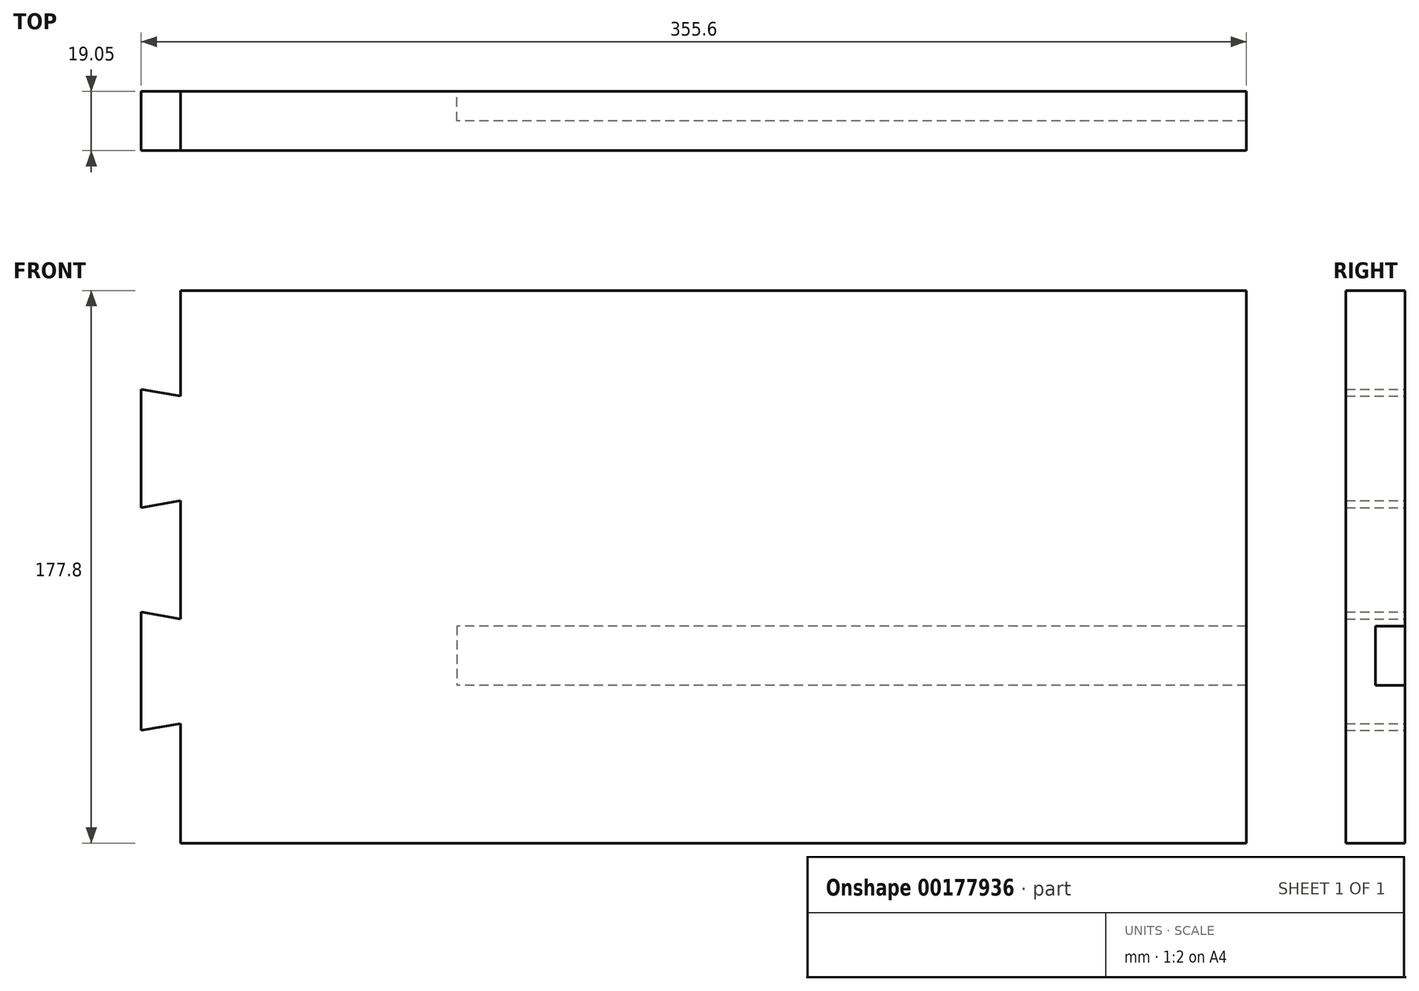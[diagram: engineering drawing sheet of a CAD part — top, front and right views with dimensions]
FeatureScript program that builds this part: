
annotation { "Feature Type Name" : "Feature", "Feature Type Description" : "" }
export const myFeature = defineFeature(function(context is Context, id is Id, definition is map)
    precondition{}
    {
        {
            var Q0;
            Q0=qCreatedBy(makeId("Front.planeOp"),FACE);
            var sketch = newSketch(context, id + "F0", { "sketchPlane" : qUnion([Q0])});
            skLineSegment(sketch, "E0.bottom", {"start": v(0, 0) * mm, "end": v(355.6, 0) * mm});
            skLineSegment(sketch, "E0.top", {"start": v(12.7, 177.8) * mm, "end": v(355.6, 177.8) * mm});
            skLineSegment(sketch, "E0.left", {"start": v(0, 36.23) * mm, "end": v(0, 74.33) * mm});
            skLineSegment(sketch, "E0.right", {"start": v(355.6, 0) * mm, "end": v(355.6, 177.8) * mm});
            skLineSegment(sketch, "E1", {"start": v(12.7, 177.8) * mm, "end": v(12.7, 143.81) * mm});
            skLineSegment(sketch, "E2", {"start": v(0, 146.05) * mm, "end": v(12.7, 143.81) * mm});
            skLineSegment(sketch, "E3", {"start": v(12.7, 110.19) * mm, "end": v(0, 107.95) * mm});
            skPoint(sketch, "E4", {"position": v(0, 88.9) * mm});
            skLineSegment(sketch, "E5", {"start": v(0, 74.33) * mm, "end": v(12.7, 72.09) * mm});
            skLineSegment(sketch, "E6", {"start": v(12.7, 38.47) * mm, "end": v(0, 36.23) * mm});
            skLineSegment(sketch, "E7.trimOffspring", {"start": v(12.7, 110.19) * mm, "end": v(12.7, 72.09) * mm});
            skLineSegment(sketch, "E8.trimOffspring", {"start": v(12.7, 38.47) * mm, "end": v(12.7, 0) * mm});
            skPoint(sketch, "E9.orphan", {"position": v(0, 177.8) * mm});
            skLineSegment(sketch, "E10.trimOffspring", {"start": v(0, 107.95) * mm, "end": v(0, 146.05) * mm});
            skSolve(sketch);
        }
        {
            var Q0;
            Q0=makeQuery(id+"F0.imprint","IMPRINT",FACE,{"disambiguationData":[TD([[makeQuery(id+"F0.imprint","IMPRINT",EDGE,{"derivedFrom":sQuery(id+"F0.wireOp",EDGE,"E0.bottom")}),1.0]])]});
            extrude(context, id + "F1", {"entities" : qUnion([Q0]), "depth" : 19.05 * mm});
        }
        {
            var Q0;
            Q0=makeQuery(id+"F1.opExtrude","CAP_FACE",FACE,{"disambiguationData":[OSD([sQuery(id+"F0.wireOp",EDGE,"E0.bottom"),sQuery(id+"F0.wireOp",EDGE,"E0.top"),sQuery(id+"F0.wireOp",EDGE,"E0.left"),sQuery(id+"F0.wireOp",EDGE,"E0.right"),sQuery(id+"F0.wireOp",EDGE,"E1"),sQuery(id+"F0.wireOp",EDGE,"E2"),sQuery(id+"F0.wireOp",EDGE,"E3"),sQuery(id+"F0.wireOp",EDGE,"E5"),sQuery(id+"F0.wireOp",EDGE,"E6"),sQuery(id+"F0.wireOp",EDGE,"E7.trimOffspring"),sQuery(id+"F0.wireOp",EDGE,"E8.trimOffspring"),sQuery(id+"F0.wireOp",EDGE,"E10.trimOffspring")])],"isStart":true});
            var sketch = newSketch(context, id + "F2", { "sketchPlane" : qUnion([Q0])});
            skLineSegment(sketch, "E11.bottom", {"start": v(-355.6, 69.85) * mm, "end": v(-101.6, 69.85) * mm});
            skLineSegment(sketch, "E11.top", {"start": v(-355.6, 50.8) * mm, "end": v(-101.6, 50.8) * mm});
            skLineSegment(sketch, "E11.left", {"start": v(-355.6, 69.85) * mm, "end": v(-355.6, 50.8) * mm});
            skLineSegment(sketch, "E11.right", {"start": v(-101.6, 69.85) * mm, "end": v(-101.6, 50.8) * mm});
            skSolve(sketch);
        }
        {
            var Q0;
            Q0=makeQuery(id+"F2.imprint","IMPRINT",FACE,{"disambiguationData":[TD([[makeQuery(id+"F2.imprint","IMPRINT",EDGE,{"derivedFrom":sQuery(id+"F2.wireOp",EDGE,"E11.bottom")}),-1.0]])]});
            extrude(context, id + "F3", {"entities" : qUnion([Q0]), "operationType" : NewBodyOperationType.REMOVE, "oppositeDirection" : true, "depth" : 9.52 * mm});
        }
    });
